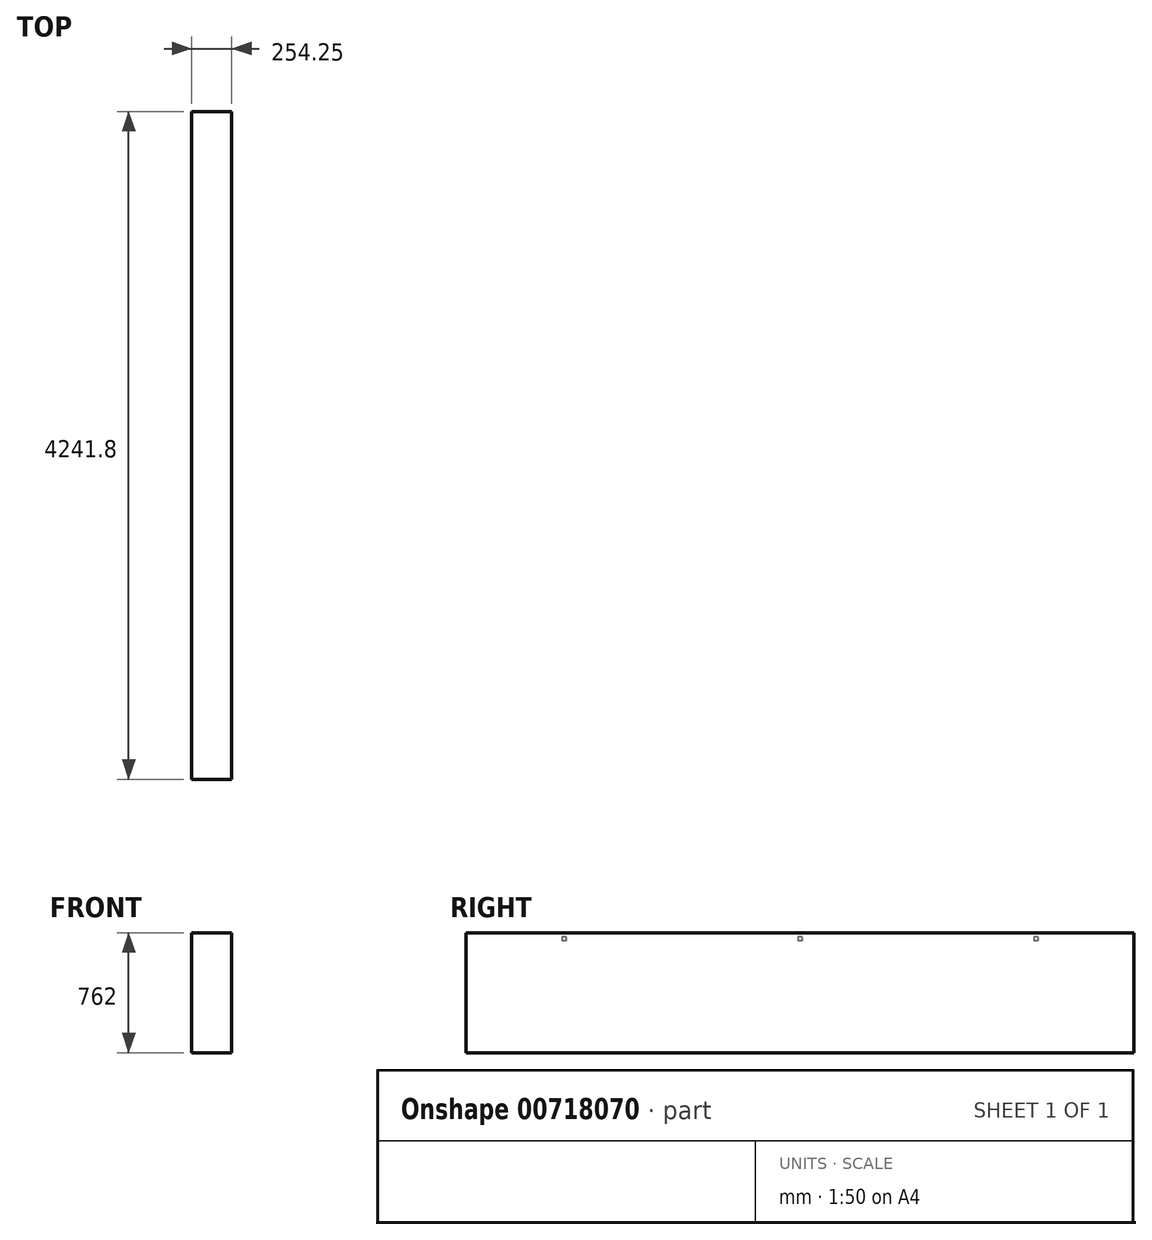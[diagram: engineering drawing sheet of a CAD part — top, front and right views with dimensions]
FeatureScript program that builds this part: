
annotation { "Feature Type Name" : "Feature", "Feature Type Description" : "" }
export const myFeature = defineFeature(function(context is Context, id is Id, definition is map)
    precondition{}
    {
        {
            var Q0;
            Q0=qCreatedBy(makeId("Front.planeOp"),FACE);
            var sketch = newSketch(context, id + "F0", { "sketchPlane" : qUnion([Q0])});
            skLineSegment(sketch, "E0.bottom", {"start": v(127, -381) * mm, "end": v(-127, -381) * mm});
            skLineSegment(sketch, "E0.top", {"start": v(127, 381) * mm, "end": v(-127, 381) * mm});
            skLineSegment(sketch, "E0.left", {"start": v(127, -381) * mm, "end": v(127, 381) * mm});
            skLineSegment(sketch, "E0.right", {"start": v(-127, -381) * mm, "end": v(-127, 381) * mm});
            skPoint(sketch, "E0.middle", {"position": v(0, 0) * mm});
            skSolve(sketch);
        }
        {
            var Q0;
            Q0=qSketchRegion(id+"F0",true);
            extrude(context, id + "F1", {"entities" : qUnion([Q0]), "depth" : 4241.8 * mm, "offsetDistance" : 25.4 * mm});
        }
        {
            var Q0;
            Q0=makeQuery(id+"F1.opExtrude","SWEPT_FACE",FACE,{"disambiguationData":[OSD([sQuery(id+"F0.wireOp",EDGE,"E0.right")])]});
            var sketch = newSketch(context, id + "F2", { "sketchPlane" : qUnion([Q0])});
            skLineSegment(sketch, "E1.bottom", {"start": v(609.6, 355.6) * mm, "end": v(635, 355.6) * mm});
            skLineSegment(sketch, "E1.top", {"start": v(609.6, 330.2) * mm, "end": v(635, 330.2) * mm});
            skLineSegment(sketch, "E1.left", {"start": v(609.6, 355.6) * mm, "end": v(609.6, 330.2) * mm});
            skLineSegment(sketch, "E1.right", {"start": v(635, 355.6) * mm, "end": v(635, 330.2) * mm});
            skLineSegment(sketch, "E2.bottom", {"start": v(2108.2, 355.6) * mm, "end": v(2133.6, 355.6) * mm});
            skLineSegment(sketch, "E2.top", {"start": v(2108.2, 330.2) * mm, "end": v(2133.6, 330.2) * mm});
            skLineSegment(sketch, "E2.left", {"start": v(2108.2, 355.6) * mm, "end": v(2108.2, 330.2) * mm});
            skLineSegment(sketch, "E2.right", {"start": v(2133.6, 355.6) * mm, "end": v(2133.6, 330.2) * mm});
            skLineSegment(sketch, "E3.bottom", {"start": v(3606.8, 355.6) * mm, "end": v(3632.2, 355.6) * mm});
            skLineSegment(sketch, "E3.top", {"start": v(3606.8, 330.2) * mm, "end": v(3632.2, 330.2) * mm});
            skLineSegment(sketch, "E3.left", {"start": v(3606.8, 355.6) * mm, "end": v(3606.8, 330.2) * mm});
            skLineSegment(sketch, "E3.right", {"start": v(3632.2, 355.6) * mm, "end": v(3632.2, 330.2) * mm});
            skSolve(sketch);
        }
        {
            var Q0;
            Q0=qSketchRegion(id+"F2",true);
            extrude(context, id + "F3", {"entities" : qUnion([Q0]), "operationType" : NewBodyOperationType.ADD, "depth" : 0.25 * mm, "offsetDistance" : 25.4 * mm});
        }
    });
